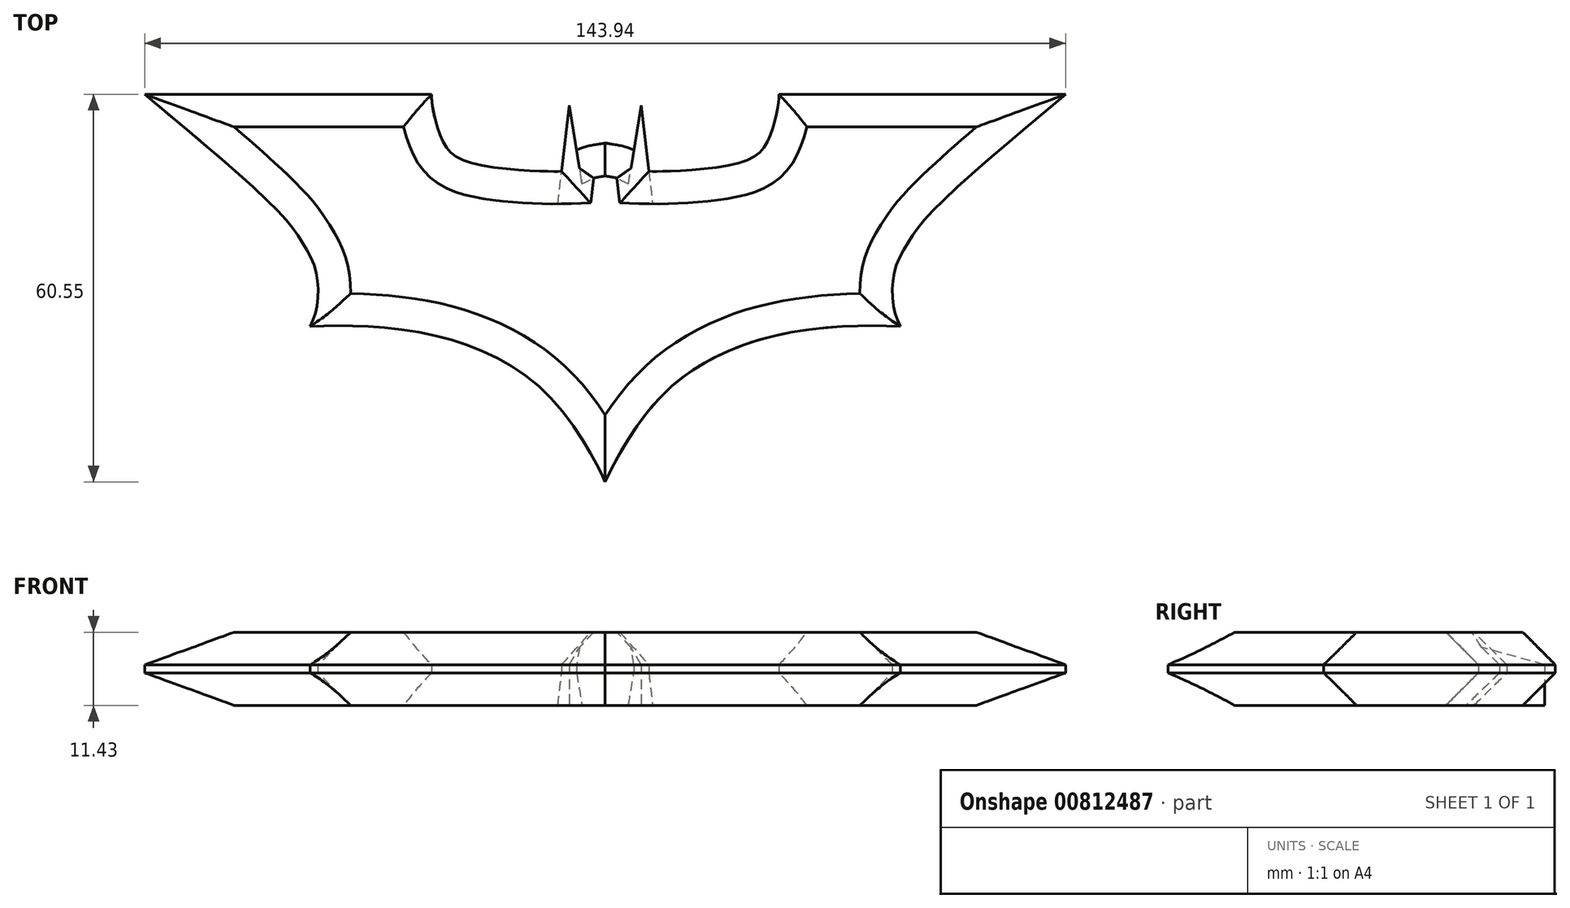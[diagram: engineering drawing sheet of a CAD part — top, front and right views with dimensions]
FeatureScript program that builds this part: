
annotation { "Feature Type Name" : "Feature", "Feature Type Description" : "" }
export const myFeature = defineFeature(function(context is Context, id is Id, definition is map)
    precondition{}
    {
        {
            var Q0;
            Q0=qCreatedBy(makeId("Top.planeOp"),FACE);
            var sketch = newSketch(context, id + "F0", { "sketchPlane" : qUnion([Q0])});
            skLineSegment(sketch, "E0", {"start": v(0, 0) * mm, "end": v(-33, 0) * mm});
            skFitSpline(sketch, "E1", {"points": [v(0, 17.3) * mm, v(-1.4, 17.06) * mm, v(-3.35, 16.66) * mm, v(-4.47, 16.18) * mm], "startDerivative": vector(-4.1, -0.71) * mm, "endDerivative": vector(-3.42, -1.73) * mm});
            skLineSegment(sketch, "E2", {"start": v(-4.47, 16.18) * mm, "end": v(-5.6, 23.2) * mm});
            skLineSegment(sketch, "E3", {"start": v(-5.6, 23.2) * mm, "end": v(-6.81, 12.87) * mm});
            skFitSpline(sketch, "E4", {"points": [v(-6.81, 12.87) * mm, v(-9.23, 12.87) * mm, v(-21.65, 14.4) * mm, v(-25.44, 17.7) * mm, v(-26.98, 22.8) * mm, v(-27.14, 24.89) * mm], "startDerivative": vector(-12.54, -0.34) * mm, "endDerivative": vector(-0.24, 13.93) * mm});
            skLineSegment(sketch, "E5", {"start": v(-27.14, 24.89) * mm, "end": v(-71.97, 24.89) * mm});
            skFitSpline(sketch, "E6", {"points": [v(-46.1, -11.34) * mm, v(-45.14, -8.77) * mm, v(-44.92, -4.9) * mm, v(-45.67, -1.37) * mm, v(-47.6, 2.16) * mm, v(-51.35, 6.88) * mm, v(-71.97, 24.89) * mm], "startDerivative": vector(10.26, 21.98) * mm, "endDerivative": vector(-72.38, 60.38) * mm});
            skFitSpline(sketch, "E7", {"points": [v(-46.1, -11.34) * mm, v(-38.06, -11.34) * mm, v(-26.96, -12.72) * mm, v(-16.86, -16.33) * mm, v(-8.01, -23.07) * mm, v(-1.9, -31.92) * mm, v(0, -35.66) * mm], "startDerivative": vector(49.03, 1.23) * mm, "endDerivative": vector(13.98, -29.3) * mm});
            skLineSegment(sketch, "E8", {"start": v(0, 17.3) * mm, "end": v(0, -35.66) * mm});
            skLineSegment(sketch, "E9.MirrorCS", {"start": v(27.14, 24.89) * mm, "end": v(71.97, 24.89) * mm});
            skFitSpline(sketch, "E10.MirrorCS", {"points": [v(46.1, -11.34) * mm, v(45.14, -8.77) * mm, v(44.92, -4.9) * mm, v(45.67, -1.37) * mm, v(47.6, 2.16) * mm, v(51.35, 6.88) * mm, v(71.97, 24.89) * mm], "startDerivative": vector(-10.26, 21.98) * mm, "endDerivative": vector(72.38, 60.38) * mm});
            skFitSpline(sketch, "E11.MirrorCS", {"points": [v(6.81, 12.87) * mm, v(9.23, 12.87) * mm, v(21.65, 14.4) * mm, v(25.44, 17.7) * mm, v(26.98, 22.8) * mm, v(27.14, 24.89) * mm], "startDerivative": vector(12.54, -0.34) * mm, "endDerivative": vector(0.24, 13.93) * mm});
            skLineSegment(sketch, "E12.MirrorCS", {"start": v(5.6, 23.2) * mm, "end": v(6.81, 12.87) * mm});
            skLineSegment(sketch, "E13.MirrorCS", {"start": v(4.47, 16.18) * mm, "end": v(5.6, 23.2) * mm});
            skFitSpline(sketch, "E14.MirrorCS", {"points": [v(0, 17.3) * mm, v(1.4, 17.06) * mm, v(3.35, 16.66) * mm, v(4.47, 16.18) * mm], "startDerivative": vector(4.1, -0.71) * mm, "endDerivative": vector(3.42, -1.73) * mm});
            skFitSpline(sketch, "E15.MirrorCS", {"points": [v(46.1, -11.34) * mm, v(38.06, -11.34) * mm, v(26.96, -12.72) * mm, v(16.86, -16.33) * mm, v(8.01, -23.07) * mm, v(1.9, -31.92) * mm, v(0, -35.66) * mm], "startDerivative": vector(-49.03, 1.23) * mm, "endDerivative": vector(-13.98, -29.3) * mm});
            skSolve(sketch);
        }
        {
            var Q0;
            {var subQ0=sQuery(id+"F0.wireOp",EDGE,"E1");Q0=makeQuery(id+"F0.imprint","IMPRINT",FACE,{"disambiguationData":[TD([[makeQuery(id+"F0.imprint","IMPRINT",EDGE,{"derivedFrom":subQ0}),1.0]])]});}
            var Q1;
            Q1=makeQuery(id+"F0.imprint","IMPRINT",FACE,{"disambiguationData":[TD([[makeQuery(id+"F0.imprint","IMPRINT",EDGE,{"derivedFrom":sQuery(id+"F0.wireOp",EDGE,"E9.MirrorCS")}),-1.0]])]});
            extrude(context, id + "F1", {"entities" : qUnion([Q0, Q1]), "depth" : 11.43 * mm, "offsetDistance" : 25 * mm});
        }
        {
            var Q0;
            Q0=makeQuery(id+"F1.opExtrude","CAP_EDGE",EDGE,{"disambiguationData":[OSD([sQuery(id+"F0.wireOp",EDGE,"E10.MirrorCS")])],"isStart":false});
            var Q1;
            Q1=makeQuery(id+"F1.opExtrude","CAP_EDGE",EDGE,{"disambiguationData":[OSD([sQuery(id+"F0.wireOp",EDGE,"E9.MirrorCS")])],"isStart":false});
            var Q2;
            Q2=makeQuery(id+"F1.opExtrude","CAP_EDGE",EDGE,{"disambiguationData":[OSD([sQuery(id+"F0.wireOp",EDGE,"E11.MirrorCS")])],"isStart":false});
            var Q3;
            Q3=makeQuery(id+"F1.opExtrude","CAP_EDGE",EDGE,{"disambiguationData":[OSD([sQuery(id+"F0.wireOp",EDGE,"E15.MirrorCS")])],"isStart":false});
            var Q4;
            Q4=makeQuery(id+"F1.opExtrude","CAP_EDGE",EDGE,{"disambiguationData":[OSD([sQuery(id+"F0.wireOp",EDGE,"E7")])],"isStart":false});
            var Q5;
            Q5=makeQuery(id+"F1.opExtrude","CAP_EDGE",EDGE,{"disambiguationData":[OSD([sQuery(id+"F0.wireOp",EDGE,"E6")])],"isStart":false});
            var Q6;
            Q6=makeQuery(id+"F1.opExtrude","CAP_EDGE",EDGE,{"disambiguationData":[OSD([sQuery(id+"F0.wireOp",EDGE,"E5")])],"isStart":false});
            var Q7;
            Q7=makeQuery(id+"F1.opExtrude","CAP_EDGE",EDGE,{"disambiguationData":[OSD([sQuery(id+"F0.wireOp",EDGE,"E4")])],"isStart":false});
            var Q8;
            Q8=makeQuery(id+"F1.opExtrude","CAP_EDGE",EDGE,{"disambiguationData":[OSD([sQuery(id+"F0.wireOp",EDGE,"E3")])],"isStart":false});
            var Q9;
            Q9=makeQuery(id+"F1.opExtrude","CAP_EDGE",EDGE,{"disambiguationData":[OSD([sQuery(id+"F0.wireOp",EDGE,"E12.MirrorCS")])],"isStart":false});
            var Q10;
            Q10=makeQuery(id+"F1.opExtrude","CAP_EDGE",EDGE,{"disambiguationData":[OSD([sQuery(id+"F0.wireOp",EDGE,"E1")])],"isStart":false});
            var Q11;
            Q11=makeQuery(id+"F1.opExtrude","CAP_EDGE",EDGE,{"disambiguationData":[OSD([sQuery(id+"F0.wireOp",EDGE,"E14.MirrorCS")])],"isStart":false});
            chamfer(context, id + "F2", {"entities" : qUnion([Q0, Q1, Q2, Q3, Q4, Q5, Q6, Q7, Q8, Q9, Q10, Q11]), "width" : 5.08 * mm, "tangentPropagation" : true});
        }
        {
            var Q0;
            Q0=makeQuery(id+"F1.opExtrude","CAP_EDGE",EDGE,{"disambiguationData":[OSD([sQuery(id+"F0.wireOp",EDGE,"E10.MirrorCS")])],"isStart":true});
            var Q1;
            Q1=makeQuery(id+"F1.opExtrude","CAP_EDGE",EDGE,{"disambiguationData":[OSD([sQuery(id+"F0.wireOp",EDGE,"E9.MirrorCS")])],"isStart":true});
            var Q2;
            Q2=makeQuery(id+"F1.opExtrude","CAP_EDGE",EDGE,{"disambiguationData":[OSD([sQuery(id+"F0.wireOp",EDGE,"E15.MirrorCS")])],"isStart":true});
            var Q3;
            Q3=makeQuery(id+"F1.opExtrude","CAP_EDGE",EDGE,{"disambiguationData":[OSD([sQuery(id+"F0.wireOp",EDGE,"E7")])],"isStart":true});
            var Q4;
            Q4=makeQuery(id+"F1.opExtrude","CAP_EDGE",EDGE,{"disambiguationData":[OSD([sQuery(id+"F0.wireOp",EDGE,"E6")])],"isStart":true});
            var Q5;
            Q5=makeQuery(id+"F1.opExtrude","CAP_EDGE",EDGE,{"disambiguationData":[OSD([sQuery(id+"F0.wireOp",EDGE,"E5")])],"isStart":true});
            var Q6;
            Q6=makeQuery(id+"F1.opExtrude","CAP_EDGE",EDGE,{"disambiguationData":[OSD([sQuery(id+"F0.wireOp",EDGE,"E4")])],"isStart":true});
            var Q7;
            Q7=makeQuery(id+"F1.opExtrude","CAP_EDGE",EDGE,{"disambiguationData":[OSD([sQuery(id+"F0.wireOp",EDGE,"E11.MirrorCS")])],"isStart":true});
            var Q8;
            Q8=makeQuery(id+"F1.opExtrude","CAP_EDGE",EDGE,{"disambiguationData":[OSD([sQuery(id+"F0.wireOp",EDGE,"E14.MirrorCS")])],"isStart":true});
            var Q9;
            Q9=makeQuery(id+"F1.opExtrude","CAP_EDGE",EDGE,{"disambiguationData":[OSD([sQuery(id+"F0.wireOp",EDGE,"E1")])],"isStart":true});
            chamfer(context, id + "F3", {"entities" : qUnion([Q0, Q1, Q2, Q3, Q4, Q5, Q6, Q7, Q8, Q9]), "width" : 5.08 * mm, "tangentPropagation" : true});
        }
    });
